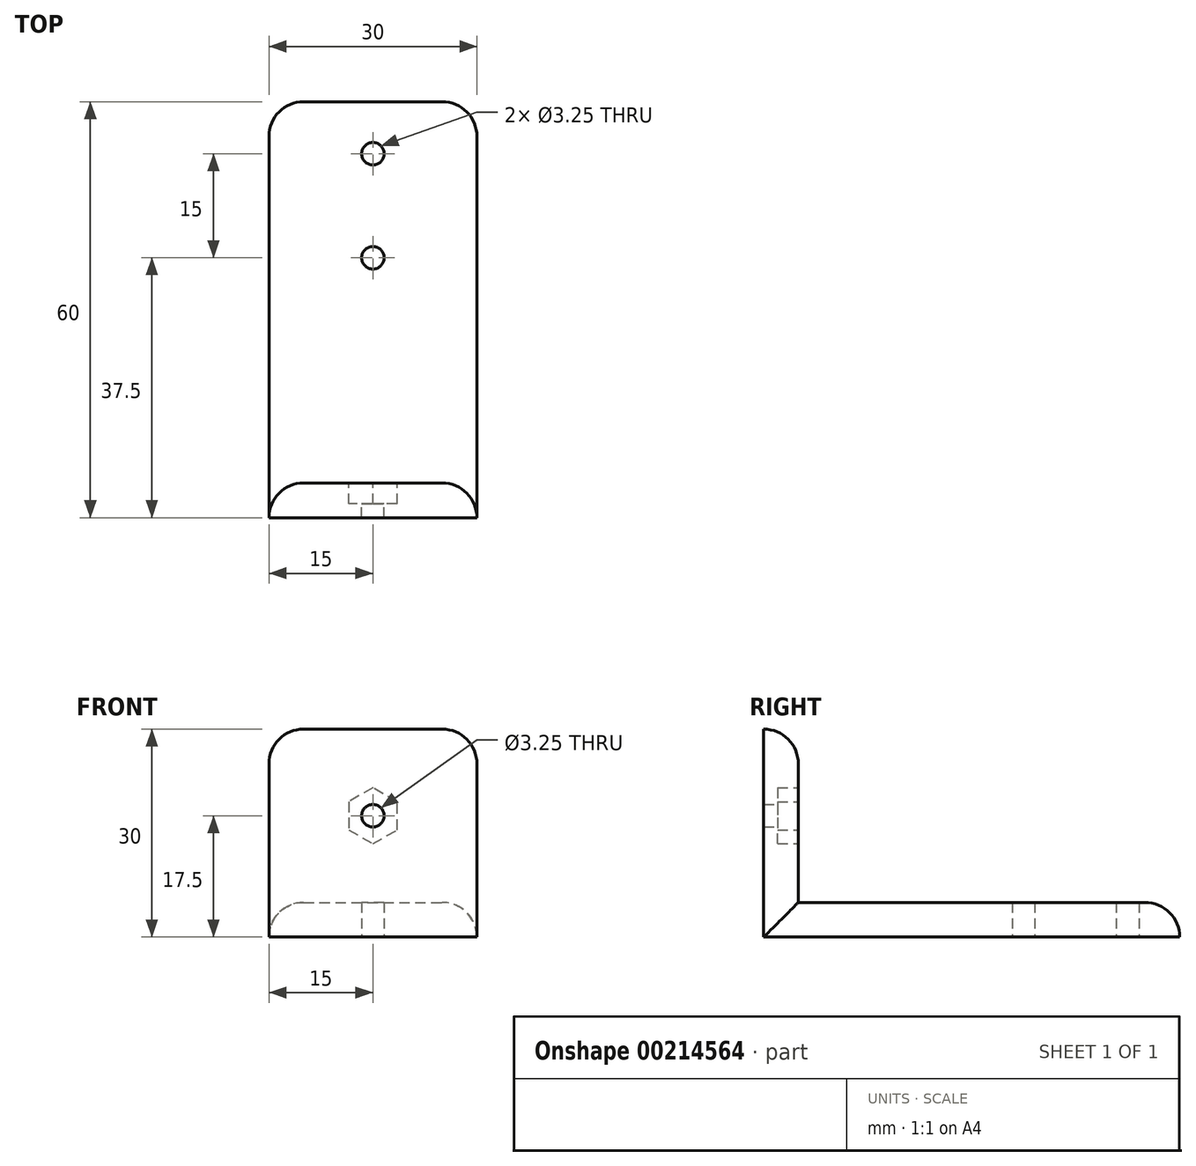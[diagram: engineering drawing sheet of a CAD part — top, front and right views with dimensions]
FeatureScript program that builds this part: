
annotation { "Feature Type Name" : "Feature", "Feature Type Description" : "" }
export const myFeature = defineFeature(function(context is Context, id is Id, definition is map)
    precondition{}
    {
        {
            var Q0;
            Q0=qCreatedBy(makeId("Top.planeOp"),FACE);
            var sketch = newSketch(context, id + "F0", { "sketchPlane" : qUnion([Q0])});
            skLineSegment(sketch, "E0.bottom", {"start": v(-15, 30) * mm, "end": v(15, 30) * mm});
            skLineSegment(sketch, "E0.top", {"start": v(-15, -30) * mm, "end": v(15, -30) * mm});
            skLineSegment(sketch, "E0.left", {"start": v(-15, 30) * mm, "end": v(-15, -30) * mm});
            skLineSegment(sketch, "E0.right", {"start": v(15, 30) * mm, "end": v(15, -30) * mm});
            skCircle(sketch, "E1", {"center": v(0, 22.5) * mm, "radius": 1.62 * mm});
            skCircle(sketch, "E2", {"center": v(0, 7.5) * mm, "radius": 1.62 * mm});
            skSolve(sketch);
        }
        {
            var Q0;
            Q0=makeQuery(id+"F0.imprint","IMPRINT",FACE,{"disambiguationData":[TD([[makeQuery(id+"F0.imprint","IMPRINT",EDGE,{"derivedFrom":sQuery(id+"F0.wireOp",EDGE,"E0.bottom")}),-1.0]])]});
            extrude(context, id + "F1", {"entities" : qUnion([Q0]), "depth" : 5 * mm});
        }
        {
            var Q0;
            Q0=makeQuery(id+"F1.opExtrude","SWEPT_FACE",FACE,{"disambiguationData":[OSD([sQuery(id+"F0.wireOp",EDGE,"E0.right")])]});
            var sketch = newSketch(context, id + "F2", { "sketchPlane" : qUnion([Q0])});
            skLineSegment(sketch, "E3.bottom", {"start": v(-30, 5) * mm, "end": v(-25, 5) * mm});
            skLineSegment(sketch, "E3.top", {"start": v(-30, 30) * mm, "end": v(-25, 30) * mm});
            skLineSegment(sketch, "E3.left", {"start": v(-30, 5) * mm, "end": v(-30, 30) * mm});
            skLineSegment(sketch, "E3.right", {"start": v(-25, 5) * mm, "end": v(-25, 30) * mm});
            skSolve(sketch);
        }
        {
            var Q0;
            Q0=makeQuery(id+"F2.imprint","IMPRINT",FACE,{"disambiguationData":[TD([[makeQuery(id+"F2.imprint","IMPRINT",EDGE,{"derivedFrom":sQuery(id+"F2.wireOp",EDGE,"E3.bottom")}),-1.0]])]});
            extrude(context, id + "F3", {"entities" : qUnion([Q0]), "operationType" : NewBodyOperationType.ADD, "oppositeDirection" : true, "depth" : 30 * mm});
        }
        {
            var Q0;
            Q0=makeQuery(id+"F3.opExtrude","SWEPT_FACE",FACE,{"disambiguationData":[OSD([sQuery(id+"F2.wireOp",EDGE,"E3.right")])]});
            var sketch = newSketch(context, id + "F4", { "sketchPlane" : qUnion([Q0])});
            skCircle(sketch, "E4", {"center": v(0, 17.5) * mm, "radius": 1.62 * mm});
            skPoint(sketch, "E4.centerSnap0", {"position": v(15, 17.5) * mm});
            skSolve(sketch);
        }
        {
            var Q0;
            Q0=makeQuery(id+"F4.imprint","IMPRINT",FACE,{"disambiguationData":[TD([[makeQuery(id+"F4.imprint","IMPRINT",EDGE,{"derivedFrom":sQuery(id+"F4.wireOp",EDGE,"E4")}),1.0]])]});
            var Q1;
            Q1=sQuery(id+"F4.wireOp",EDGE,"E4");
            extrude(context, id + "F5", {"entities" : qUnion([Q0]), "operationType" : NewBodyOperationType.REMOVE, "surfaceEntities" : qUnion([Q1]), "oppositeDirection" : true, "depth" : 25 * mm});
        }
        {
            var Q0;
            Q0=makeQuery(id+"F3.opExtrude","SWEPT_FACE",FACE,{"disambiguationData":[OSD([sQuery(id+"F2.wireOp",EDGE,"E3.right")])]});
            var sketch = newSketch(context, id + "F6", { "sketchPlane" : qUnion([Q0])});
            skCircle(sketch, "E5.cCircle", {"center": v(0, 17.5) * mm, "radius": 3.5 * mm, "construction": true});
            skLineSegment(sketch, "E5.0", {"start": v(3.5, 19.52) * mm, "end": v(3.5, 15.48) * mm});
            skLineSegment(sketch, "E5.1", {"start": v(3.5, 15.48) * mm, "end": v(0, 13.46) * mm});
            skLineSegment(sketch, "E5.2", {"start": v(0, 13.46) * mm, "end": v(-3.5, 15.48) * mm});
            skLineSegment(sketch, "E5.3", {"start": v(-3.5, 15.48) * mm, "end": v(-3.5, 19.52) * mm});
            skLineSegment(sketch, "E5.4", {"start": v(-3.5, 19.52) * mm, "end": v(0, 21.54) * mm});
            skLineSegment(sketch, "E5.5", {"start": v(0, 21.54) * mm, "end": v(3.5, 19.52) * mm});
            skPoint(sketch, "E5.0.midPoint", {"position": v(3.5, 17.5) * mm});
            skSolve(sketch);
        }
        {
            var Q0;
            Q0=makeQuery(id+"F6.imprint","IMPRINT",FACE,{"disambiguationData":[TD([[makeQuery(id+"F6.imprint","IMPRINT",EDGE,{"derivedFrom":sQuery(id+"F6.wireOp",EDGE,"E5.0")}),-1.0]])]});
            extrude(context, id + "F7", {"entities" : qUnion([Q0]), "operationType" : NewBodyOperationType.REMOVE, "oppositeDirection" : true, "depth" : 3 * mm});
        }
        {
            var Q0;
            Q0=makeQuery(id+"F1.opExtrude","CAP_EDGE",EDGE,{"disambiguationData":[OSD([sQuery(id+"F0.wireOp",EDGE,"E0.bottom")])],"isStart":false});
            var Q1;
            Q1=makeQuery(id+"F1.opExtrude","SWEPT_EDGE",EDGE,{"disambiguationData":[OSD([sQuery(id+"F0.wireOp",EDGE,"E0.bottom"),sQuery(id+"F0.wireOp",EDGE,"E0.right")])]});
            var Q2;
            Q2=makeQuery(id+"F1.opExtrude","SWEPT_EDGE",EDGE,{"disambiguationData":[OSD([sQuery(id+"F0.wireOp",EDGE,"E0.bottom"),sQuery(id+"F0.wireOp",EDGE,"E0.left")])]});
            var Q3;
            Q3=makeQuery(id+"F1.opExtrude","CAP_EDGE",EDGE,{"disambiguationData":[OSD([sQuery(id+"F0.wireOp",EDGE,"E0.right")])],"isStart":false});
            var Q4;
            Q4=makeQuery(id+"F1.opExtrude","CAP_EDGE",EDGE,{"disambiguationData":[OSD([sQuery(id+"F0.wireOp",EDGE,"E0.left")])],"isStart":false});
            var Q5;
            Q5=makeQuery(id+"F3.opExtrude","CAP_EDGE",EDGE,{"disambiguationData":[OSD([sQuery(id+"F2.wireOp",EDGE,"E3.right")])],"isStart":false});
            var Q6;
            Q6=makeQuery(id+"F3.opExtrude","SWEPT_EDGE",EDGE,{"disambiguationData":[OSD([sQuery(id+"F2.wireOp",EDGE,"E3.top"),sQuery(id+"F2.wireOp",EDGE,"E3.right")])]});
            var Q7;
            Q7=makeQuery(id+"F3.opExtrude","CAP_EDGE",EDGE,{"disambiguationData":[OSD([sQuery(id+"F2.wireOp",EDGE,"E3.right")])],"isStart":true});
            var Q8;
            Q8=makeQuery(id+"F3.opExtrude","CAP_EDGE",EDGE,{"disambiguationData":[OSD([sQuery(id+"F2.wireOp",EDGE,"E3.top")])],"isStart":false});
            var Q9;
            Q9=makeQuery(id+"F3.opExtrude","CAP_EDGE",EDGE,{"disambiguationData":[OSD([sQuery(id+"F2.wireOp",EDGE,"E3.top")])],"isStart":true});
            fillet(context, id + "F8", {"entities" : qUnion([Q0, Q1, Q2, Q3, Q4, Q5, Q6, Q7, Q8, Q9]), "radius" : 5 * mm, "tangentPropagation" : true, "allowEdgeOverflow" : false});
        }
    });
